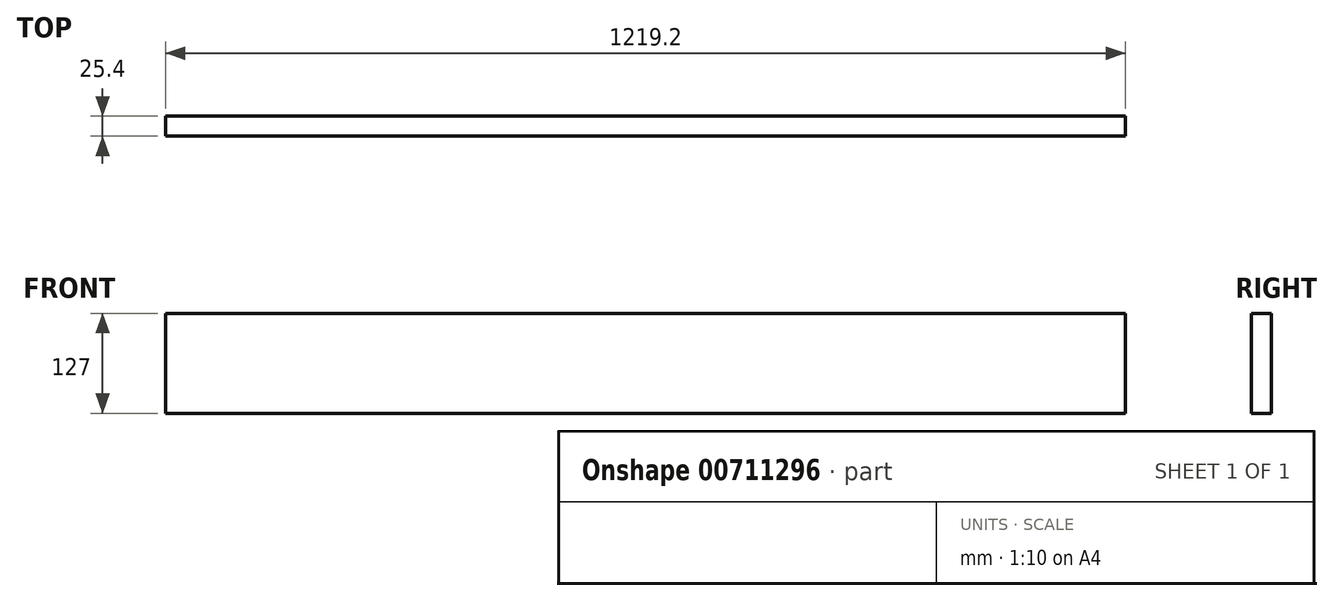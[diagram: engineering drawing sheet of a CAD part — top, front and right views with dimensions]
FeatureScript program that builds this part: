
annotation { "Feature Type Name" : "Feature", "Feature Type Description" : "" }
export const myFeature = defineFeature(function(context is Context, id is Id, definition is map)
    precondition{}
    {
        {
            var Q0;
            Q0=qCreatedBy(makeId("Front.planeOp"),FACE);
            var sketch = newSketch(context, id + "F0", { "sketchPlane" : qUnion([Q0])});
            skLineSegment(sketch, "E0.bottom", {"start": v(-603.15, -143.81) * mm, "end": v(616.05, -143.81) * mm});
            skLineSegment(sketch, "E0.top", {"start": v(-603.15, -270.81) * mm, "end": v(616.05, -270.81) * mm});
            skLineSegment(sketch, "E0.left", {"start": v(-603.15, -143.81) * mm, "end": v(-603.15, -270.81) * mm});
            skLineSegment(sketch, "E0.right", {"start": v(616.05, -143.81) * mm, "end": v(616.05, -270.81) * mm});
            skSolve(sketch);
        }
        {
            var Q0;
            Q0 = qSketchRegion(id + "F0", true);
            extrude(context, id + "F1", {"entities" : qUnion([Q0]), "endBound" : BoundingType.SYMMETRIC, "depth" : 25.4 * mm, "offsetDistance" : 25.4 * mm});
        }
    });
